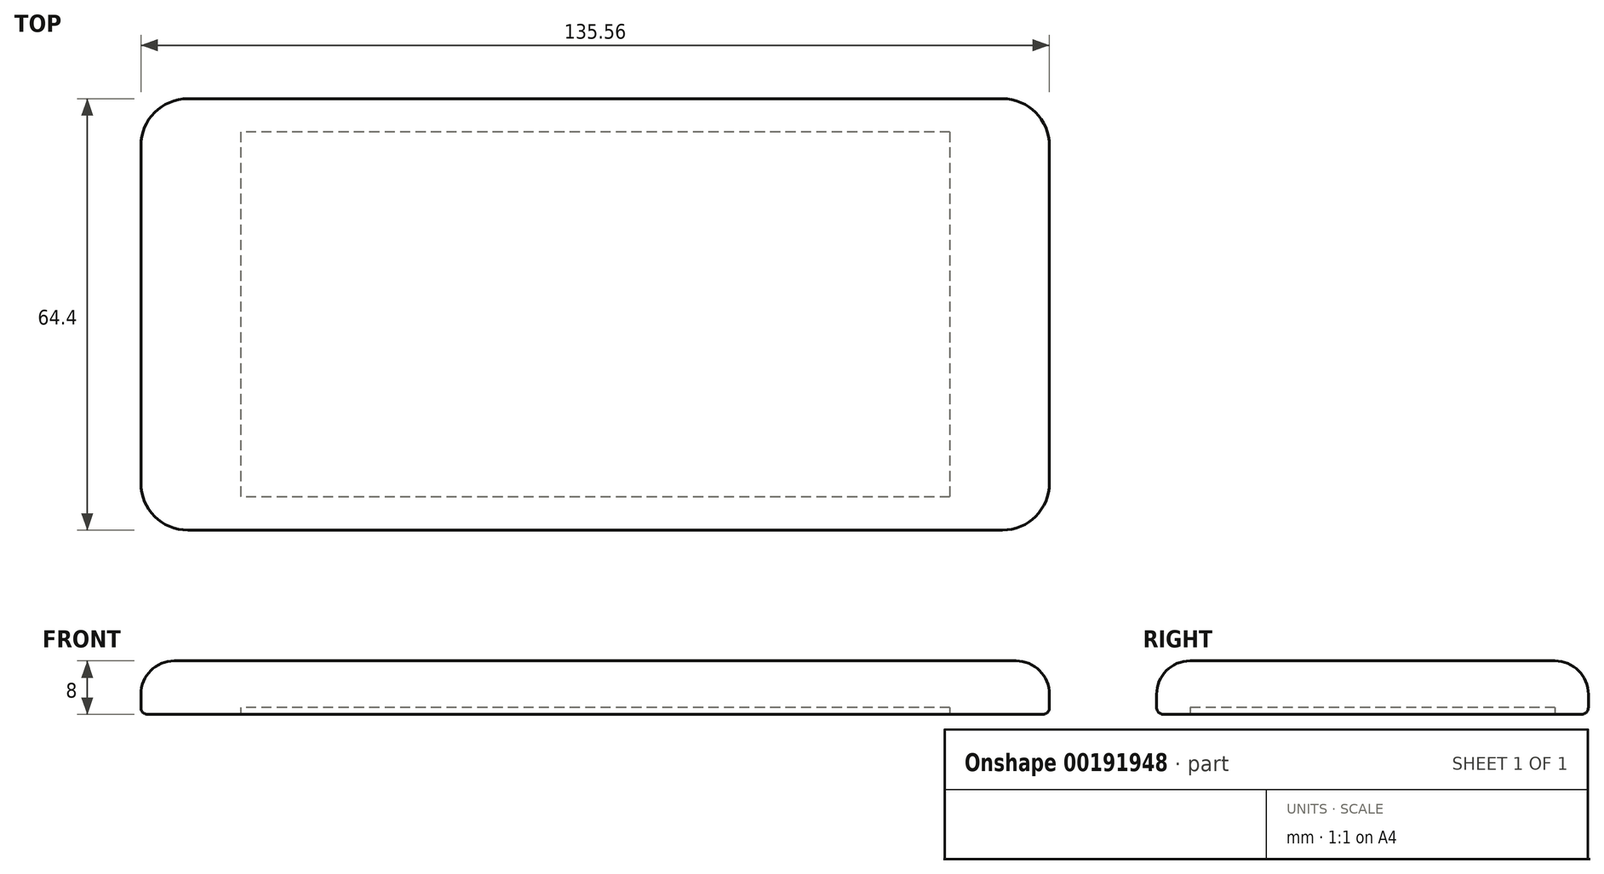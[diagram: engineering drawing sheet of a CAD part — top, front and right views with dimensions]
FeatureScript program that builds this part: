
annotation { "Feature Type Name" : "Feature", "Feature Type Description" : "" }
export const myFeature = defineFeature(function(context is Context, id is Id, definition is map)
    precondition{}
    {
        {
            var Q0;
            Q0=qCreatedBy(makeId("Top.planeOp"),FACE);
            var sketch = newSketch(context, id + "F0", { "sketchPlane" : qUnion([Q0])});
            skLineSegment(sketch, "E0.bottom", {"start": v(-67.78, -32.2) * mm, "end": v(67.78, -32.2) * mm});
            skLineSegment(sketch, "E0.top", {"start": v(-67.78, 32.2) * mm, "end": v(67.78, 32.2) * mm});
            skLineSegment(sketch, "E0.left", {"start": v(-67.78, -32.2) * mm, "end": v(-67.78, 32.2) * mm});
            skLineSegment(sketch, "E0.right", {"start": v(67.78, -32.2) * mm, "end": v(67.78, 32.2) * mm});
            skPoint(sketch, "E0.middle", {"position": v(0, 0) * mm});
            skSolve(sketch);
        }
        {
            var Q0;
            Q0 = qSketchRegion(id + "F0", true);
            extrude(context, id + "F1", {"entities" : qUnion([Q0]), "depth" : 8 * mm});
        }
        {
            var Q0;
            Q0=makeQuery(id+"F1.opExtrude","CAP_EDGE",EDGE,{"disambiguationData":[OSD([sQuery(id+"F0.wireOp",EDGE,"E0.top")])],"isStart":false});
            var Q1;
            Q1=makeQuery(id+"F1.opExtrude","CAP_EDGE",EDGE,{"disambiguationData":[OSD([sQuery(id+"F0.wireOp",EDGE,"E0.left")])],"isStart":false});
            var Q2;
            Q2=makeQuery(id+"F1.opExtrude","CAP_EDGE",EDGE,{"disambiguationData":[OSD([sQuery(id+"F0.wireOp",EDGE,"E0.bottom")])],"isStart":false});
            var Q3;
            Q3=makeQuery(id+"F1.opExtrude","CAP_EDGE",EDGE,{"disambiguationData":[OSD([sQuery(id+"F0.wireOp",EDGE,"E0.right")])],"isStart":false});
            fillet(context, id + "F2", {"entities" : qUnion([Q0, Q1, Q2, Q3]), "radius" : 5 * mm, "tangentPropagation" : true, "allowEdgeOverflow" : false});
        }
        {
            var Q0;
            Q0=makeQuery(id+"F2.opFillet","BLEND_EDGE",EDGE,{"blendedFrom":[makeQuery(id+"F1.opExtrude","CAP_EDGE",EDGE,{"disambiguationData":[OSD([sQuery(id+"F0.wireOp",EDGE,"E0.top")])],"isStart":false}),makeQuery(id+"F1.opExtrude","CAP_EDGE",EDGE,{"disambiguationData":[OSD([sQuery(id+"F0.wireOp",EDGE,"E0.left")])],"isStart":false})],"blendedInto":[]});
            var Q1;
            Q1=makeQuery(id+"F2.opFillet","BLEND_EDGE",EDGE,{"blendedFrom":[makeQuery(id+"F1.opExtrude","CAP_EDGE",EDGE,{"disambiguationData":[OSD([sQuery(id+"F0.wireOp",EDGE,"E0.top")])],"isStart":false}),makeQuery(id+"F1.opExtrude","CAP_EDGE",EDGE,{"disambiguationData":[OSD([sQuery(id+"F0.wireOp",EDGE,"E0.right")])],"isStart":false})],"blendedInto":[]});
            var Q2;
            Q2=makeQuery(id+"F2.opFillet","BLEND_EDGE",EDGE,{"blendedFrom":[makeQuery(id+"F1.opExtrude","CAP_EDGE",EDGE,{"disambiguationData":[OSD([sQuery(id+"F0.wireOp",EDGE,"E0.bottom")])],"isStart":false}),makeQuery(id+"F1.opExtrude","CAP_EDGE",EDGE,{"disambiguationData":[OSD([sQuery(id+"F0.wireOp",EDGE,"E0.right")])],"isStart":false})],"blendedInto":[]});
            var Q3;
            Q3=makeQuery(id+"F2.opFillet","BLEND_EDGE",EDGE,{"blendedFrom":[makeQuery(id+"F1.opExtrude","CAP_EDGE",EDGE,{"disambiguationData":[OSD([sQuery(id+"F0.wireOp",EDGE,"E0.bottom")])],"isStart":false}),makeQuery(id+"F1.opExtrude","CAP_EDGE",EDGE,{"disambiguationData":[OSD([sQuery(id+"F0.wireOp",EDGE,"E0.left")])],"isStart":false})],"blendedInto":[]});
            fillet(context, id + "F3", {"entities" : qUnion([Q0, Q1, Q2, Q3]), "radius" : 7 * mm, "tangentPropagation" : true, "allowEdgeOverflow" : false});
        }
        {
            var Q0;
            Q0=makeQuery(id+"F1.opExtrude","CAP_EDGE",EDGE,{"disambiguationData":[OSD([sQuery(id+"F0.wireOp",EDGE,"E0.bottom")])],"isStart":true});
            var Q1;
            Q1=makeQuery(id+"F1.opExtrude","CAP_EDGE",EDGE,{"disambiguationData":[OSD([sQuery(id+"F0.wireOp",EDGE,"E0.left")])],"isStart":true});
            fillet(context, id + "F4", {"entities" : qUnion([Q0, Q1]), "radius" : 1 * mm, "tangentPropagation" : true, "allowEdgeOverflow" : false});
        }
        {
            var Q0;
            Q0=makeQuery(id+"F1.opExtrude","CAP_FACE",FACE,{"disambiguationData":[OSD([sQuery(id+"F0.wireOp",EDGE,"E0.bottom"),sQuery(id+"F0.wireOp",EDGE,"E0.top"),sQuery(id+"F0.wireOp",EDGE,"E0.left"),sQuery(id+"F0.wireOp",EDGE,"E0.right")])],"isStart":true});
            var sketch = newSketch(context, id + "F5", { "sketchPlane" : qUnion([Q0])});
            skLineSegment(sketch, "E1.bottom", {"start": v(52.91, -27.23) * mm, "end": v(-52.91, -27.23) * mm});
            skLineSegment(sketch, "E1.top", {"start": v(52.91, 27.23) * mm, "end": v(-52.91, 27.23) * mm});
            skLineSegment(sketch, "E1.left", {"start": v(52.91, -27.23) * mm, "end": v(52.91, 27.23) * mm});
            skLineSegment(sketch, "E1.right", {"start": v(-52.91, -27.23) * mm, "end": v(-52.91, 27.23) * mm});
            skPoint(sketch, "E1.middle", {"position": v(0, 0) * mm});
            skSolve(sketch);
        }
        {
            var Q0;
            Q0=makeQuery(id+"F5.imprint","IMPRINT",FACE,{"disambiguationData":[TD([[makeQuery(id+"F5.imprint","IMPRINT",EDGE,{"derivedFrom":sQuery(id+"F5.wireOp",EDGE,"E1.bottom")}),-1.0]])]});
            extrude(context, id + "F6", {"entities" : qUnion([Q0]), "operationType" : NewBodyOperationType.REMOVE, "oppositeDirection" : true, "depth" : 1 * mm});
        }
    });
